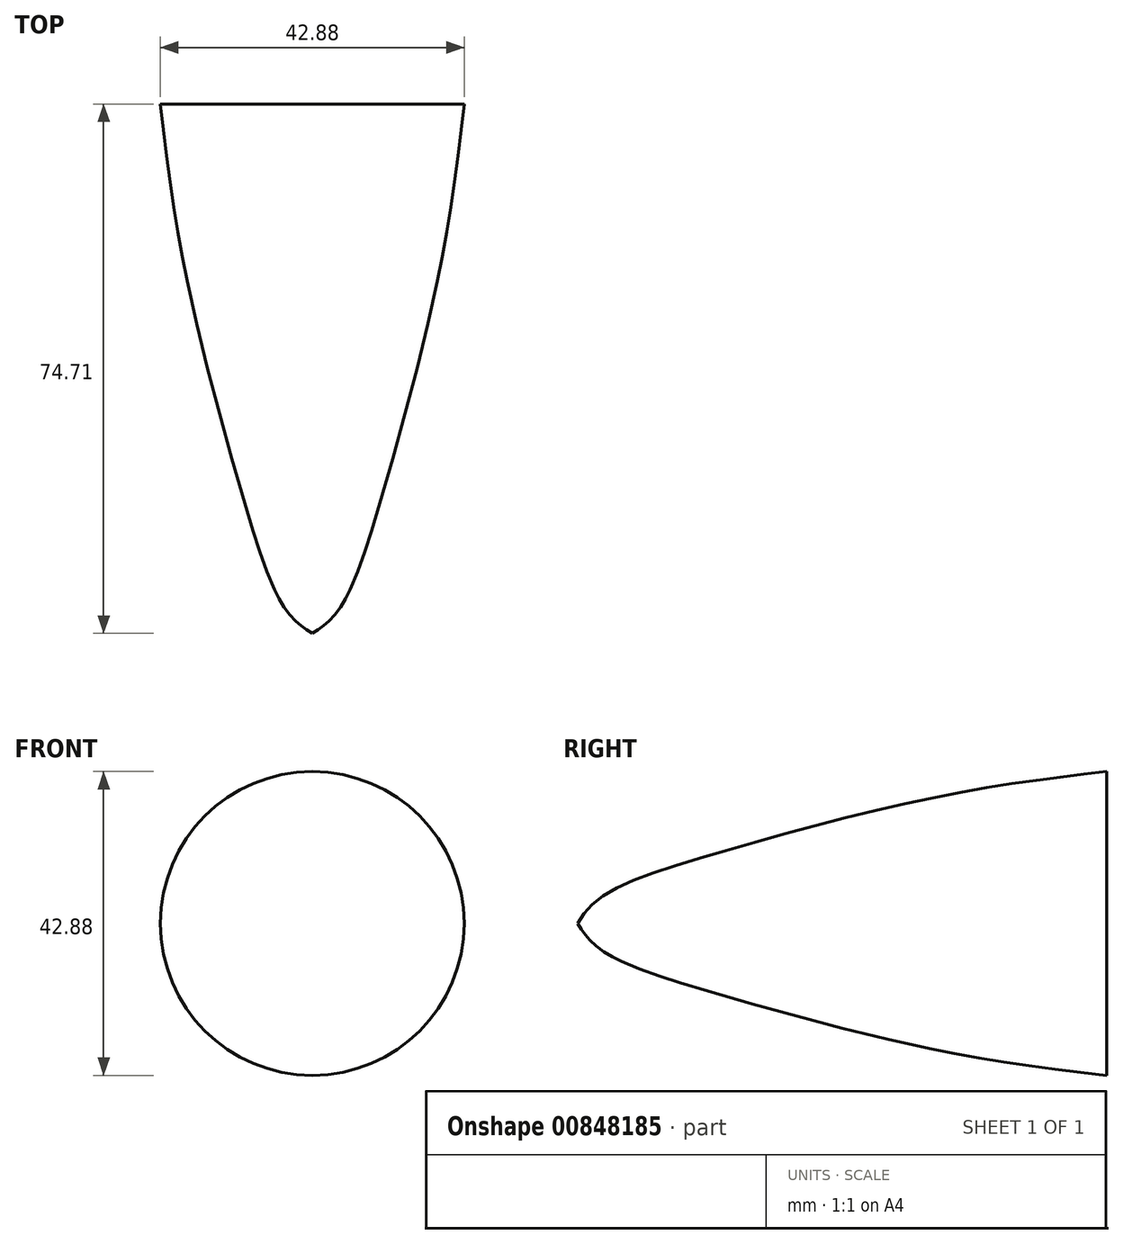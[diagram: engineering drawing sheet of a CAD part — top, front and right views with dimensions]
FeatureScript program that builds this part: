
annotation { "Feature Type Name" : "Feature", "Feature Type Description" : "" }
export const myFeature = defineFeature(function(context is Context, id is Id, definition is map)
    precondition{}
    {
        {
            var Q0;
            Q0=qCreatedBy(makeId("Front.planeOp"),FACE);
            var sketch = newSketch(context, id + "F0", { "sketchPlane" : qUnion([Q0])});
            skCircle(sketch, "E0", {"center": v(0, 0) * mm, "radius": 21.46 * mm});
            skSolve(sketch);
        }
        {
            var Q0;
            Q0=qCreatedBy(makeId("Right.planeOp"),FACE);
            var sketch = newSketch(context, id + "F1", { "sketchPlane" : qUnion([Q0])});
            skFitSpline(sketch, "E1", {"points": [v(0, 21.44) * mm, v(-13.74, 19.66) * mm, v(-32.12, 16.08) * mm, v(-54.33, 10.1) * mm, v(-67.46, 5.81) * mm, v(-72.56, 2.75) * mm, v(-74.71, 0) * mm], "startDerivative": vector(-74.97, -8.7) * mm, "endDerivative": vector(-20.67, -31.62) * mm});
            skLineSegment(sketch, "E2", {"start": v(0, 21.44) * mm, "end": v(0, 0) * mm});
            skLineSegment(sketch, "E3", {"start": v(0, 0) * mm, "end": v(-74.71, 0) * mm});
            skSolve(sketch);
        }
        {
            var Q0;
            Q0=makeQuery(id+"F1.imprint","IMPRINT",FACE,{"disambiguationData":[TD([[makeQuery(id+"F1.imprint","IMPRINT",EDGE,{"derivedFrom":sQuery(id+"F1.wireOp",EDGE,"E1")}),1.0]])]});
            var Q1;
            Q1=sQuery(id+"F1.wireOp",EDGE,"E3");
            revolve(context, id + "F2", {"surfaceOperationType" : NewSurfaceOperationType.NEW, "entities" : qUnion([Q0]), "axis" : qUnion([Q1]), "revolveType" : RevolveType.FULL});
        }
    });
